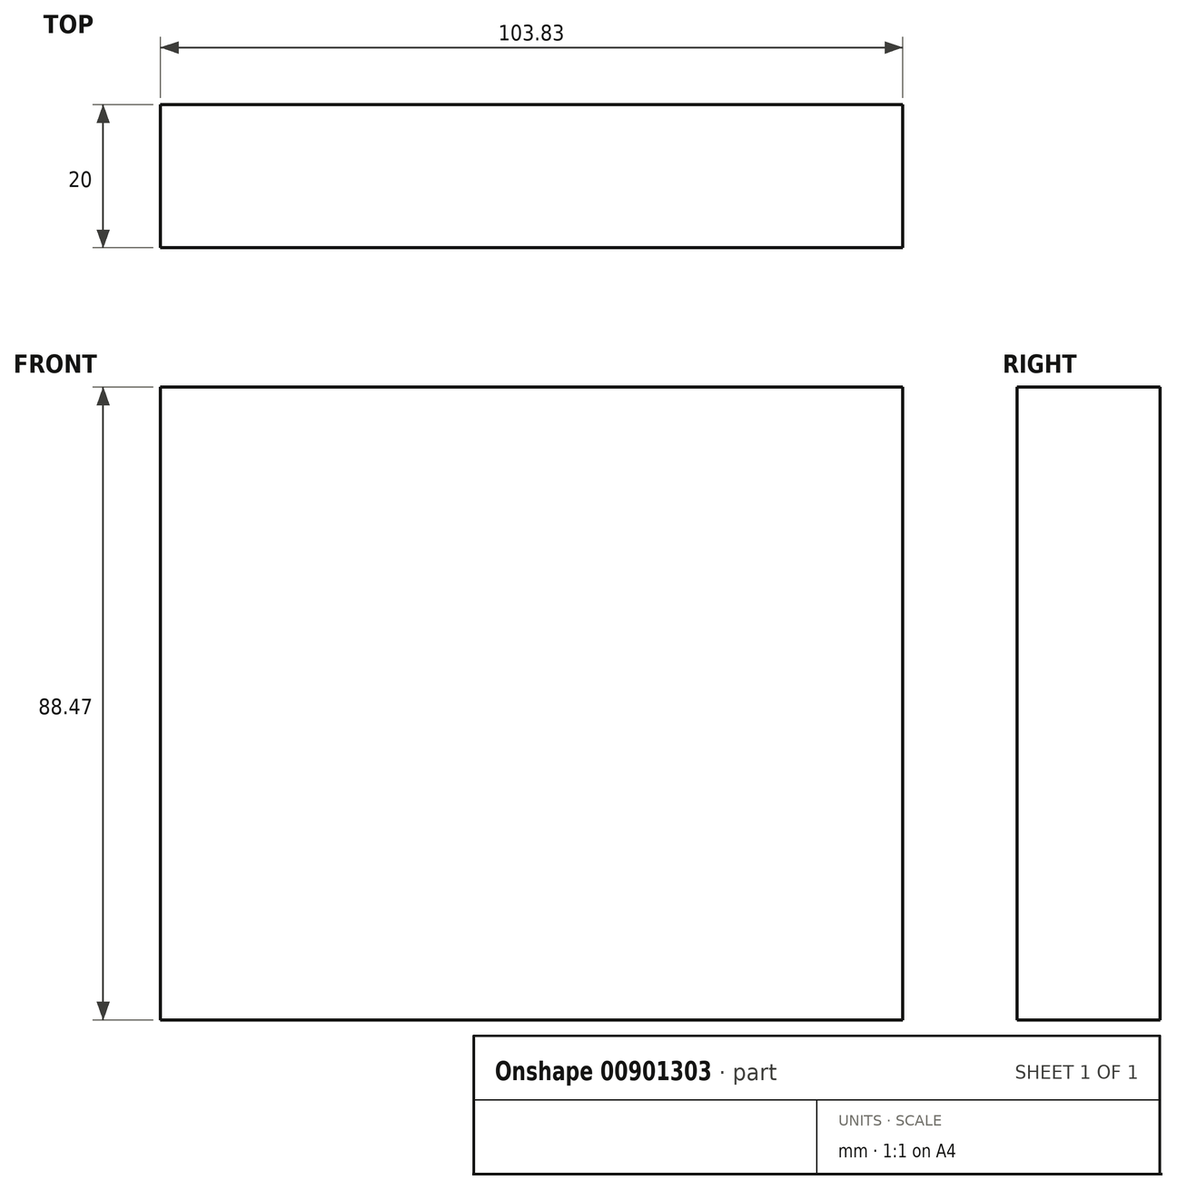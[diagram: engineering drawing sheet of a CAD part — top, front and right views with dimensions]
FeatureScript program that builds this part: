
annotation { "Feature Type Name" : "Feature", "Feature Type Description" : "" }
export const myFeature = defineFeature(function(context is Context, id is Id, definition is map)
    precondition{}
    {
        {
            var Q0;
            Q0=qCreatedBy(makeId("Front.planeOp"),FACE);
            var sketch = newSketch(context, id + "F0", { "sketchPlane" : qUnion([Q0])});
            skLineSegment(sketch, "E0.bottom", {"start": v(-53.45, 44.26) * mm, "end": v(50.38, 44.26) * mm});
            skLineSegment(sketch, "E0.top", {"start": v(-53.45, -44.2) * mm, "end": v(50.38, -44.2) * mm});
            skLineSegment(sketch, "E0.left", {"start": v(-53.45, 44.26) * mm, "end": v(-53.45, -44.2) * mm});
            skLineSegment(sketch, "E0.right", {"start": v(50.38, 44.26) * mm, "end": v(50.38, -44.2) * mm});
            skSolve(sketch);
        }
        {
            var Q0;
            Q0=makeQuery(id+"F0.imprint","IMPRINT",FACE,{"disambiguationData":[TD([[makeQuery(id+"F0.imprint","IMPRINT",EDGE,{"derivedFrom":sQuery(id+"F0.wireOp",EDGE,"E0.bottom")}),-1.0]])]});
            extrude(context, id + "F1", {"entities" : qUnion([Q0]), "depth" : 20 * mm, "offsetDistance" : 25 * mm});
        }
    });
